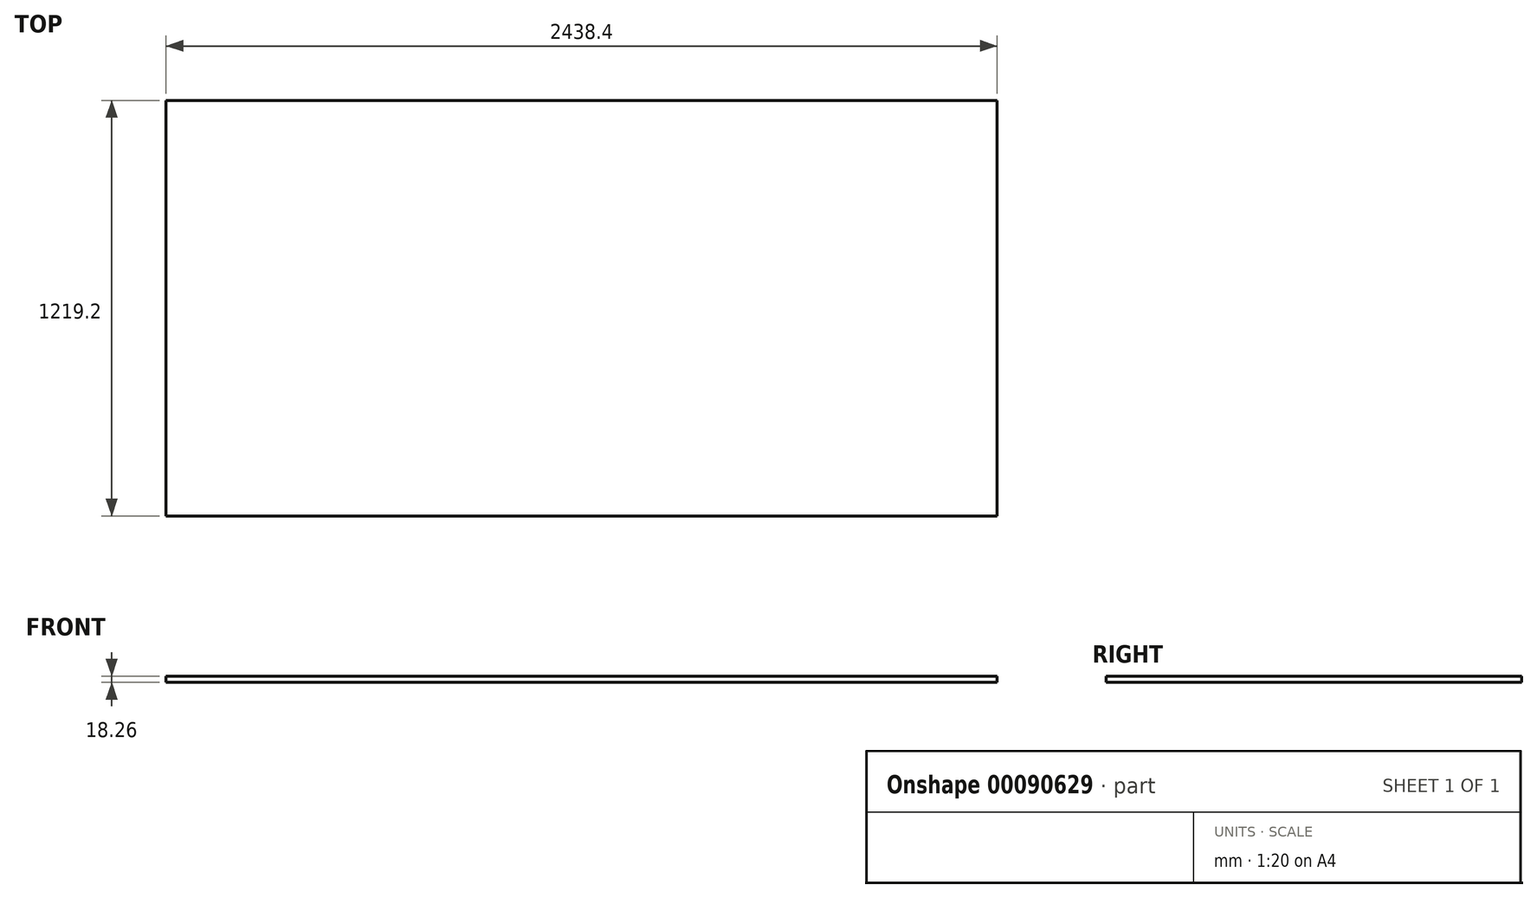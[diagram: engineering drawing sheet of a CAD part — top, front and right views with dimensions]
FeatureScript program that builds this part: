
annotation { "Feature Type Name" : "Feature", "Feature Type Description" : "" }
export const myFeature = defineFeature(function(context is Context, id is Id, definition is map)
    precondition{}
    {
        {
            var Q0;
            Q0=qCreatedBy(makeId("Top.planeOp"),FACE);
            var sketch = newSketch(context, id + "F0", { "sketchPlane" : qUnion([Q0])});
            skLineSegment(sketch, "E0.bottom", {"start": v(1219.2, 609.6) * mm, "end": v(-1219.2, 609.6) * mm});
            skLineSegment(sketch, "E0.top", {"start": v(1219.2, -609.6) * mm, "end": v(-1219.2, -609.6) * mm});
            skLineSegment(sketch, "E0.left", {"start": v(1219.2, 609.6) * mm, "end": v(1219.2, -609.6) * mm});
            skLineSegment(sketch, "E0.right", {"start": v(-1219.2, 609.6) * mm, "end": v(-1219.2, -609.6) * mm});
            skPoint(sketch, "E0.middle", {"position": v(0, 0) * mm});
            skSolve(sketch);
        }
        {
            var Q0;
            Q0=makeQuery(id+"F0.imprint","IMPRINT",FACE,{"disambiguationData":[TD([[makeQuery(id+"F0.imprint","IMPRINT",EDGE,{"derivedFrom":sQuery(id+"F0.wireOp",EDGE,"E0.bottom")}),1.0]])]});
            extrude(context, id + "F1", {"entities" : qUnion([Q0]), "depth" : 18.26 * mm});
        }
    });
